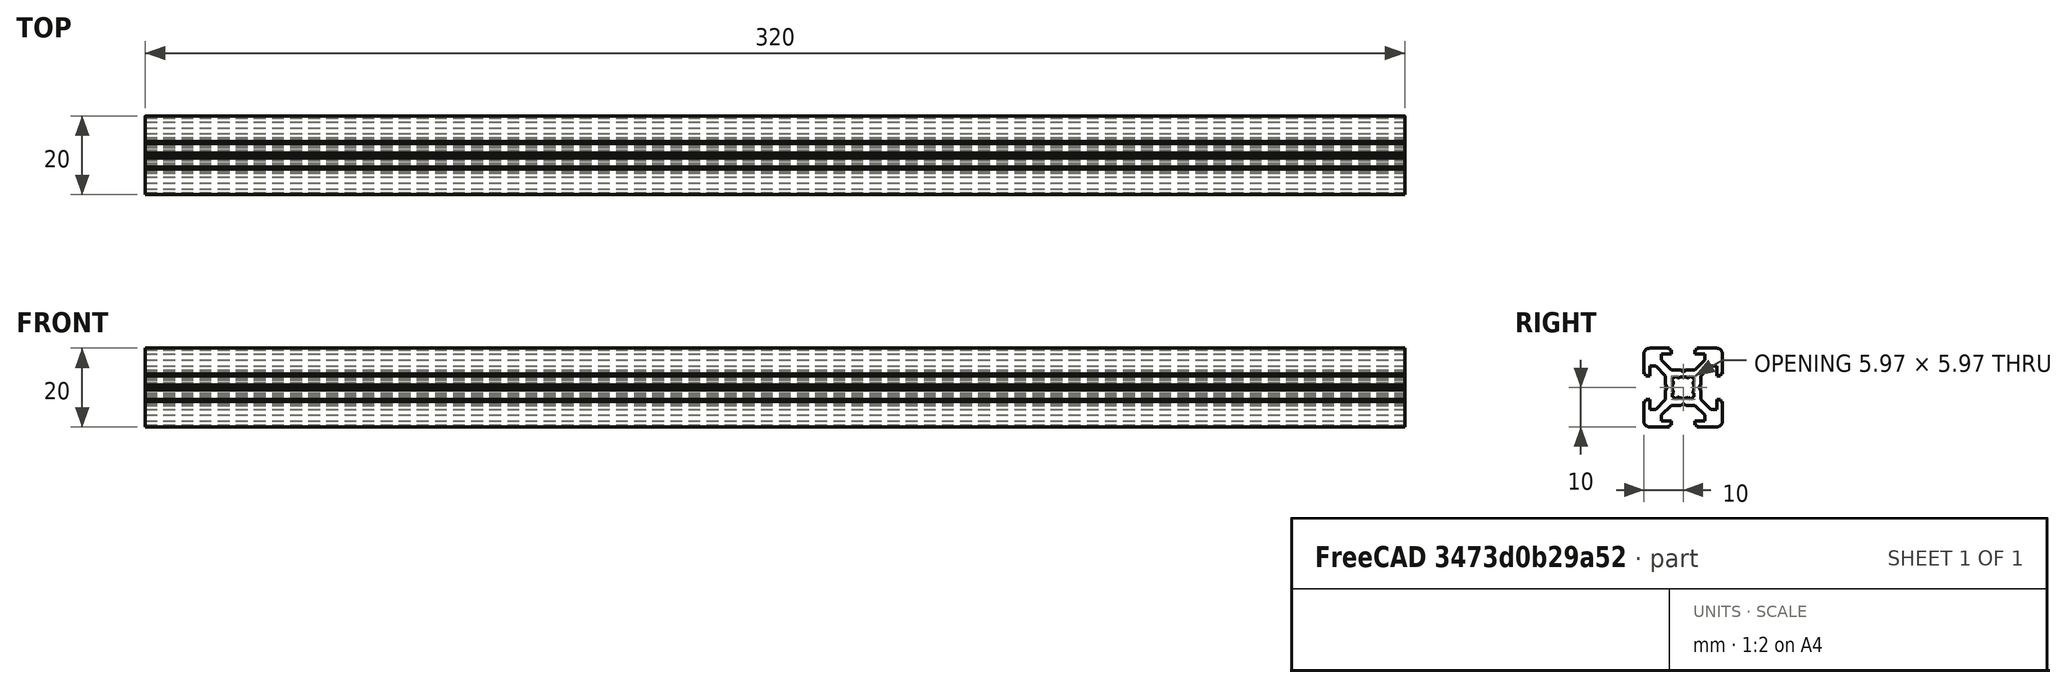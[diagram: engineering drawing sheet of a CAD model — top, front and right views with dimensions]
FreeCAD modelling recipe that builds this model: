
FCSTD DOCUMENT  (FreeCAD 0.19R)
Label: Tslot32
License: All rights reserved
LicenseURL: http://en.wikipedia.org/wiki/All_rights_reserved
objects: Sketcher::SketchObject×1, PartDesign::Pad×1, PartDesign::Body×1
note: 4 computed .brp shape members not serialized (recipe doc carries the construction recipe); baked Part::Feature solids carry a one-line shape summary decoded from their .brp

FEATURE [Sketcher::SketchObject] Sketch  label="T-Slot-Skizze"
  FullyConstrained = true
  MapMode = 5
  Placement = pos=(0,0,0) rot=(0.57735,0.57735,0.57735;2.0944rad)
  Support = -> [YZ_Plane]
  sketch-geometry (98):
    g0: LineSegment StartX=0 StartY=4.1 StartZ=0 EndX=0.65 EndY=4.5 EndZ=0
    g1: LineSegment StartX=0.65 StartY=4.5 StartZ=0 EndX=3 EndY=4.5 EndZ=0
    g2: LineSegment StartX=3 StartY=4.5 StartZ=0 EndX=5.5 EndY=7 EndZ=0
    g3: LineSegment StartX=5.5 StartY=7 StartZ=0 EndX=5.5 EndY=8.5 EndZ=0
    g4: LineSegment StartX=5.5 StartY=8.5 StartZ=0 EndX=3 EndY=8.5 EndZ=0
    g5: LineSegment StartX=3 StartY=8.5 StartZ=0 EndX=3 EndY=9.5 EndZ=0
    g6: LineSegment StartX=3 StartY=9.5 StartZ=0 EndX=3.5 EndY=9.5 EndZ=0
    g7: LineSegment StartX=3.5 StartY=9.5 StartZ=0 EndX=3.5 EndY=10 EndZ=0
    g8: LineSegment StartX=3.5 StartY=10 StartZ=0 EndX=8.5 EndY=10 EndZ=0
    g9: LineSegment StartX=10 StartY=8.5 StartZ=0 EndX=10 EndY=3.5 EndZ=0
    g10: LineSegment StartX=10 StartY=3.5 StartZ=0 EndX=9.5 EndY=3.5 EndZ=0
    g11: LineSegment StartX=9.5 StartY=3.5 StartZ=0 EndX=9.5 EndY=3 EndZ=0
    g12: LineSegment StartX=9.5 StartY=3 StartZ=0 EndX=8.5 EndY=3 EndZ=0
    g13: LineSegment StartX=8.5 StartY=3 StartZ=0 EndX=8.5 EndY=5.5 EndZ=0
    g14: LineSegment StartX=8.5 StartY=5.5 StartZ=0 EndX=7 EndY=5.5 EndZ=0
    g15: LineSegment StartX=7 StartY=5.5 StartZ=0 EndX=4.5 EndY=3 EndZ=0
    g16: LineSegment StartX=4.5 StartY=3 StartZ=0 EndX=4.5 EndY=0.65 EndZ=0
    g17: LineSegment StartX=4.5 StartY=0.65 StartZ=0 EndX=4.1 EndY=0 EndZ=0
    g18: ArcOfCircle CenterX=8.5 CenterY=8.5 CenterZ=0 NormalX=0 NormalY=0 NormalZ=1 AngleXU=0 Radius=1.5 StartAngle=0 EndAngle=1.5708
    g19: LineSegment StartX=0 StartY=-4.1 StartZ=0 EndX=0.65 EndY=-4.5 EndZ=0
    g20: LineSegment StartX=0.65 StartY=-4.5 StartZ=0 EndX=3 EndY=-4.5 EndZ=0
    g21: LineSegment StartX=3 StartY=-4.5 StartZ=0 EndX=5.5 EndY=-7 EndZ=0
    g22: LineSegment StartX=5.5 StartY=-7 StartZ=0 EndX=5.5 EndY=-8.5 EndZ=0
    g23: LineSegment StartX=5.5 StartY=-8.5 StartZ=0 EndX=3 EndY=-8.5 EndZ=0
    g24: LineSegment StartX=3 StartY=-8.5 StartZ=0 EndX=3 EndY=-9.5 EndZ=0
    g25: LineSegment StartX=3 StartY=-9.5 StartZ=0 EndX=3.5 EndY=-9.5 EndZ=0
    g26: LineSegment StartX=3.5 StartY=-9.5 StartZ=0 EndX=3.5 EndY=-10 EndZ=0
    g27: LineSegment StartX=3.5 StartY=-10 StartZ=0 EndX=8.5 EndY=-10 EndZ=0
    g28: LineSegment StartX=10 StartY=-8.5 StartZ=0 EndX=10 EndY=-3.5 EndZ=0
    g29: LineSegment StartX=10 StartY=-3.5 StartZ=0 EndX=9.5 EndY=-3.5 EndZ=0
    g30: LineSegment StartX=9.5 StartY=-3.5 StartZ=0 EndX=9.5 EndY=-3 EndZ=0
    g31: LineSegment StartX=9.5 StartY=-3 StartZ=0 EndX=8.5 EndY=-3 EndZ=0
    g32: LineSegment StartX=8.5 StartY=-3 StartZ=0 EndX=8.5 EndY=-5.5 EndZ=0
    g33: LineSegment StartX=8.5 StartY=-5.5 StartZ=0 EndX=7 EndY=-5.5 EndZ=0
    g34: LineSegment StartX=7 StartY=-5.5 StartZ=0 EndX=4.5 EndY=-3 EndZ=0
    g35: LineSegment StartX=4.5 StartY=-3 StartZ=0 EndX=4.5 EndY=-0.65 EndZ=0
    g36: ArcOfCircle CenterX=8.5 CenterY=-8.5 CenterZ=0 NormalX=0 NormalY=0 NormalZ=1 AngleXU=0 Radius=1.5 StartAngle=4.71239 EndAngle=6.28319
    g37: LineSegment StartX=4.5 StartY=-0.65 StartZ=0 EndX=4.1 EndY=0 EndZ=0
    g38: LineSegment StartX=0 StartY=-4.1 StartZ=0 EndX=-0.65 EndY=-4.5 EndZ=0
    g39: LineSegment StartX=-0.65 StartY=-4.5 StartZ=0 EndX=-3 EndY=-4.5 EndZ=0
    g40: LineSegment StartX=-3 StartY=-4.5 StartZ=0 EndX=-5.5 EndY=-7 EndZ=0
    g41: LineSegment StartX=-5.5 StartY=-7 StartZ=0 EndX=-5.5 EndY=-8.5 EndZ=0
    g42: LineSegment StartX=-5.5 StartY=-8.5 StartZ=0 EndX=-3 EndY=-8.5 EndZ=0
    g43: LineSegment StartX=-3 StartY=-8.5 StartZ=0 EndX=-3 EndY=-9.5 EndZ=0
    g44: LineSegment StartX=-3 StartY=-9.5 StartZ=0 EndX=-3.5 EndY=-9.5 EndZ=0
    g45: LineSegment StartX=-3.5 StartY=-9.5 StartZ=0 EndX=-3.5 EndY=-10 EndZ=0
    g46: LineSegment StartX=-3.5 StartY=-10 StartZ=0 EndX=-8.5 EndY=-10 EndZ=0
    g47: LineSegment StartX=-10 StartY=-8.5 StartZ=0 EndX=-10 EndY=-3.5 EndZ=0
    g48: LineSegment StartX=-10 StartY=-3.5 StartZ=0 EndX=-9.5 EndY=-3.5 EndZ=0
    g49: LineSegment StartX=-9.5 StartY=-3.5 StartZ=0 EndX=-9.5 EndY=-3 EndZ=0
    g50: LineSegment StartX=-9.5 StartY=-3 StartZ=0 EndX=-8.5 EndY=-3 EndZ=0
    g51: LineSegment StartX=-8.5 StartY=-3 StartZ=0 EndX=-8.5 EndY=-5.5 EndZ=0
    g52: LineSegment StartX=-8.5 StartY=-5.5 StartZ=0 EndX=-7 EndY=-5.5 EndZ=0
    g53: LineSegment StartX=-7 StartY=-5.5 StartZ=0 EndX=-4.5 EndY=-3 EndZ=0
    g54: LineSegment StartX=-4.5 StartY=-3 StartZ=0 EndX=-4.5 EndY=-0.65 EndZ=0
    g55: ArcOfCircle CenterX=-8.5 CenterY=-8.5 CenterZ=0 NormalX=0 NormalY=0 NormalZ=1 AngleXU=0 Radius=1.5 StartAngle=3.14159 EndAngle=4.71239
    g56: LineSegment StartX=-4.5 StartY=-0.65 StartZ=0 EndX=-4.1 EndY=0 EndZ=0
    g57: LineSegment StartX=-0.65 StartY=4.5 StartZ=0 EndX=-3 EndY=4.5 EndZ=0
    g58: LineSegment StartX=-3 StartY=4.5 StartZ=0 EndX=-5.5 EndY=7 EndZ=0
    g59: LineSegment StartX=-5.5 StartY=7 StartZ=0 EndX=-5.5 EndY=8.5 EndZ=0
    g60: LineSegment StartX=-5.5 StartY=8.5 StartZ=0 EndX=-3 EndY=8.5 EndZ=0
    g61: LineSegment StartX=-3 StartY=8.5 StartZ=0 EndX=-3 EndY=9.5 EndZ=0
    g62: LineSegment StartX=-3 StartY=9.5 StartZ=0 EndX=-3.5 EndY=9.5 EndZ=0
    g63: LineSegment StartX=-3.5 StartY=9.5 StartZ=0 EndX=-3.5 EndY=10 EndZ=0
    g64: LineSegment StartX=-3.5 StartY=10 StartZ=0 EndX=-8.5 EndY=10 EndZ=0
    g65: LineSegment StartX=-10 StartY=8.5 StartZ=0 EndX=-10 EndY=3.5 EndZ=0
    g66: LineSegment StartX=-10 StartY=3.5 StartZ=0 EndX=-9.5 EndY=3.5 EndZ=0
    g67: LineSegment StartX=-9.5 StartY=3.5 StartZ=0 EndX=-9.5 EndY=3 EndZ=0
    g68: LineSegment StartX=-9.5 StartY=3 StartZ=0 EndX=-8.5 EndY=3 EndZ=0
    g69: LineSegment StartX=-8.5 StartY=3 StartZ=0 EndX=-8.5 EndY=5.5 EndZ=0
    g70: LineSegment StartX=-8.5 StartY=5.5 StartZ=0 EndX=-7 EndY=5.5 EndZ=0
    g71: LineSegment StartX=-7 StartY=5.5 StartZ=0 EndX=-4.5 EndY=3 EndZ=0
    g72: LineSegment StartX=-4.5 StartY=3 StartZ=0 EndX=-4.5 EndY=0.65 EndZ=0
    g73: ArcOfCircle CenterX=-8.5 CenterY=8.5 CenterZ=0 NormalX=0 NormalY=0 NormalZ=1 AngleXU=0 Radius=1.5 StartAngle=1.5708 EndAngle=3.14159
    g74: LineSegment StartX=-4.5 StartY=0.65 StartZ=0 EndX=-4.1 EndY=0 EndZ=0
    g75: LineSegment StartX=0 StartY=4.1 StartZ=0 EndX=-0.65 EndY=4.5 EndZ=0
    g76: Circle CenterX=0 CenterY=0 CenterZ=0 NormalX=0 NormalY=0 NormalZ=1 AngleXU=0 Radius=3.55
    g77: Circle CenterX=0 CenterY=0 CenterZ=0 NormalX=0 NormalY=0 NormalZ=1 AngleXU=0 Radius=2.75
    g78: LineSegment StartX=1.3405 StartY=2.40116 StartZ=0 EndX=1.92324 EndY=2.9839 EndZ=0
    g79: LineSegment StartX=1.92324 StartY=2.9839 StartZ=0 EndX=2.9839 EndY=1.92324 EndZ=0
    g80: LineSegment StartX=2.9839 StartY=1.92324 StartZ=0 EndX=2.40116 EndY=1.3405 EndZ=0
    g81: ArcOfCircle CenterX=0 CenterY=0 CenterZ=0 NormalX=0 NormalY=0 NormalZ=1 AngleXU=0 Radius=2.75 StartAngle=0 EndAngle=0.509172
    g82: ArcOfCircle CenterX=0 CenterY=0 CenterZ=0 NormalX=0 NormalY=0 NormalZ=1 AngleXU=0 Radius=2.75 StartAngle=1.06162 EndAngle=1.5708
    g83: LineSegment StartX=-1.3405 StartY=2.40116 StartZ=0 EndX=-1.92324 EndY=2.9839 EndZ=0
    g84: LineSegment StartX=-1.92324 StartY=2.9839 StartZ=0 EndX=-2.9839 EndY=1.92324 EndZ=0
    g85: LineSegment StartX=-2.9839 StartY=1.92324 StartZ=0 EndX=-2.40116 EndY=1.3405 EndZ=0
    g86: ArcOfCircle CenterX=-1.3e-15 CenterY=6e-16 CenterZ=0 NormalX=0 NormalY=0 NormalZ=1 AngleXU=0 Radius=2.75 StartAngle=2.63242 EndAngle=3.14159
    g87: ArcOfCircle CenterX=-1.3e-15 CenterY=6e-16 CenterZ=0 NormalX=0 NormalY=0 NormalZ=1 AngleXU=0 Radius=2.75 StartAngle=1.5708 EndAngle=2.07997
    g88: LineSegment StartX=-1.34051 StartY=-2.40115 StartZ=0 EndX=-1.92325 EndY=-2.98389 EndZ=0
    g89: LineSegment StartX=-1.92325 StartY=-2.98389 StartZ=0 EndX=-2.9839 EndY=-1.92323 EndZ=0
    g90: LineSegment StartX=-2.9839 StartY=-1.92323 StartZ=0 EndX=-2.40116 EndY=-1.34049 EndZ=0
    g91: ArcOfCircle CenterX=-3e-16 CenterY=2e-16 CenterZ=0 NormalX=0 NormalY=0 NormalZ=1 AngleXU=0 Radius=2.75 StartAngle=3.14159 EndAngle=3.65076
    g92: ArcOfCircle CenterX=-3e-16 CenterY=2e-16 CenterZ=0 NormalX=0 NormalY=0 NormalZ=1 AngleXU=0 Radius=2.75 StartAngle=4.20321 EndAngle=4.71239
    g93: LineSegment StartX=1.34051 StartY=-2.40115 StartZ=0 EndX=1.92325 EndY=-2.98389 EndZ=0
    g94: LineSegment StartX=1.92325 StartY=-2.98389 StartZ=0 EndX=2.9839 EndY=-1.92323 EndZ=0
    g95: LineSegment StartX=2.9839 StartY=-1.92323 StartZ=0 EndX=2.40116 EndY=-1.34049 EndZ=0
    g96: ArcOfCircle CenterX=3e-16 CenterY=2e-16 CenterZ=0 NormalX=0 NormalY=0 NormalZ=1 AngleXU=0 Radius=2.75 StartAngle=4.71239 EndAngle=5.22156
    g97: ArcOfCircle CenterX=3e-16 CenterY=2e-16 CenterZ=0 NormalX=0 NormalY=0 NormalZ=1 AngleXU=0 Radius=2.75 StartAngle=5.77402 EndAngle=6.28319
  constraints (291):
    c: PointOnObject(g0,g-2)
    c: Coincident(g0,g1)
    c: Horizontal(g1)
    c: Coincident(g1,g2)
    c: Coincident(g2,g3)
    c: Vertical(g3)
    c: Coincident(g3,g4)
    c: Horizontal(g4)
    c: Coincident(g4,g5)
    c: Vertical(g5)
    c: Coincident(g5,g6)
    c: Horizontal(g6)
    c: Coincident(g6,g7)
    c: Coincident(g7,g8)
    c: Horizontal(g8)
    c: Vertical(g7)
    c: DistanceX(g-1,g5) = 3
    c: DistanceY(g4,g7) = 1.5
    c: DistanceY(g0,g7) = 5.5
    c: DistanceY(g3,g3) = 1.5
    c: DistanceY(g4,g5) = 1
    c: DistanceX(g-1,g1) = 3
    c: DistanceX(g-1,g7) = 3.5
    c: DistanceX(g0,g0) = 0.65
    c: DistanceY(g0,g0) = 0.4
    c: DistanceX(g-1,g3) = 5.5
    c: Vertical(g9)
    c: Coincident(g9,g10)
    c: Coincident(g10,g11)
    c: Coincident(g11,g12)
    c: Coincident(g12,g13)
    c: Vertical(g13)
    c: Coincident(g13,g14)
    c: Horizontal(g14)
    c: Coincident(g14,g15)
    c: Coincident(g15,g16)
    c: Vertical(g16)
    c: Coincident(g16,g17)
    c: PointOnObject(g17,g-1)
    c: Horizontal(g10)
    c: Horizontal(g12)
    c: Vertical(g11)
    c: Equal(g17,g0)
    c: Equal(g1,g16)
    c: Equal(g15,g2)
    c: Equal(g3,g14)
    c: Equal(g13,g4)
    c: Equal(g12,g5)
    c: Parallel(g15,g2)
    c: Equal(g11,g6)
    c: Equal(g10,g7)
    c: Equal(g9,g8)
    c: Tangent(g8,g18) = 1.5708
    c: Tangent(g9,g18) = 1.5708
    c: Radius(g18) = 1.5
    c: DistanceY(g-1,g8) = 10
    c: DistanceX(g-1,g9) = 10
    c: Coincident(g19,g20)
    c: Horizontal(g20)
    c: Coincident(g20,g21)
    c: Coincident(g21,g22)
    c: Vertical(g22)
    c: Coincident(g22,g23)
    c: Horizontal(g23)
    c: Coincident(g23,g24)
    c: Vertical(g24)
    c: Coincident(g24,g25)
    c: Horizontal(g25)
    c: Coincident(g25,g26)
    c: Coincident(g26,g27)
    c: Horizontal(g27)
    c: Vertical(g26)
    c: Vertical(g28)
    c: Coincident(g28,g29)
    c: Coincident(g29,g30)
    c: Coincident(g30,g31)
    c: Coincident(g31,g32)
    c: Vertical(g32)
    c: Coincident(g32,g33)
    c: Horizontal(g33)
    c: Coincident(g33,g34)
    c: Coincident(g34,g35)
    c: Vertical(g35)
    c: Coincident(g35,g37)
    c: Horizontal(g29)
    c: Horizontal(g31)
    c: Vertical(g30)
    c: Equal(g37,g19)
    c: Equal(g20,g35)
    c: Equal(g34,g21)
    c: Equal(g22,g33)
    c: Equal(g32,g23)
    c: Equal(g31,g24)
    c: Parallel(g34,g21)
    c: Equal(g30,g25)
    c: Equal(g29,g26)
    c: Equal(g28,g27)
    c: Tangent(g27,g36) = -1.5708
    c: Tangent(g28,g36) = -1.5708
    c: Radius(g36) = 1.5
    c: Equal(g9,g28)
    c: Equal(g12,g31)
    c: DistanceX(g-1,g28) = 10
    c: DistanceY(g27,g-1) = 10
    c: DistanceY(g30,g-1) = 3
    c: Equal(g33,g14)
    c: Equal(g35,g16)
    c: Equal(g17,g37)
    c: Coincident(g37,g17)
    c: Equal(g15,g34)
    c: PointOnObject(g19,g-2)
    c: DistanceY(g34,g-1) = 3
    c: DistanceX(g-1,g20) = 3
    c: Coincident(g38,g39)
    c: Horizontal(g39)
    c: Coincident(g39,g40)
    c: Coincident(g40,g41)
    c: Vertical(g41)
    c: Coincident(g41,g42)
    c: Horizontal(g42)
    c: Coincident(g42,g43)
    c: Vertical(g43)
    c: Coincident(g43,g44)
    c: Horizontal(g44)
    c: Coincident(g44,g45)
    c: Coincident(g45,g46)
    c: Horizontal(g46)
    c: Vertical(g45)
    c: Vertical(g47)
    c: Coincident(g47,g48)
    c: Coincident(g48,g49)
    c: Coincident(g49,g50)
    c: Coincident(g50,g51)
    c: Vertical(g51)
    c: Coincident(g51,g52)
    c: Horizontal(g52)
    c: Coincident(g52,g53)
    c: Coincident(g53,g54)
    c: Vertical(g54)
    c: Coincident(g54,g56)
    c: Horizontal(g48)
    c: Horizontal(g50)
    c: Vertical(g49)
    c: Equal(g39,g54)
    c: Equal(g53,g40)
    c: Equal(g41,g52)
    c: Equal(g51,g42)
    c: Equal(g50,g43)
    c: Parallel(g53,g40)
    c: Equal(g49,g44)
    c: Equal(g48,g45)
    c: Equal(g47,g46)
    c: Tangent(g46,g55) = 1.5708
    c: Tangent(g47,g55) = 1.5708
    c: Radius(g55) = 1.5
    c: Coincident(g38,g19)
    c: DistanceX(g39,g-1) = 3
    c: DistanceX(g38,g19) = 0.65
    c: DistanceY(g38,g19) = 0.4
    c: PointOnObject(g56,g-1)
    c: Equal(g56,g38)
    c: DistanceY(g53,g-1) = 3
    c: Equal(g22,g41)
    c: Equal(g42,g23)
    c: Equal(g24,g43)
    c: Equal(g25,g44)
    c: Equal(g26,g45)
    c: DistanceY(g46,g-1) = 10
    c: DistanceX(g47,g-1) = 10
    c: Coincident(g75,g57)
    c: Horizontal(g57)
    c: Coincident(g57,g58)
    c: Coincident(g58,g59)
    c: Vertical(g59)
    c: Coincident(g59,g60)
    c: Horizontal(g60)
    c: Coincident(g60,g61)
    c: Vertical(g61)
    c: Coincident(g61,g62)
    c: Horizontal(g62)
    c: Coincident(g62,g63)
    c: Coincident(g63,g64)
    c: Horizontal(g64)
    c: Vertical(g63)
    c: Vertical(g65)
    c: Coincident(g65,g66)
    c: Coincident(g66,g67)
    c: Coincident(g67,g68)
    c: Coincident(g68,g69)
    c: Vertical(g69)
    c: Coincident(g69,g70)
    c: Horizontal(g70)
    c: Coincident(g70,g71)
    c: Coincident(g71,g72)
    c: Vertical(g72)
    c: Coincident(g72,g74)
    c: Horizontal(g66)
    c: Horizontal(g68)
    c: Vertical(g67)
    c: Equal(g57,g72)
    c: Equal(g71,g58)
    c: Equal(g59,g70)
    c: Equal(g69,g60)
    c: Equal(g68,g61)
    c: Parallel(g71,g58)
    c: Equal(g67,g62)
    c: Equal(g66,g63)
    c: Equal(g65,g64)
    c: Tangent(g64,g73) = -1.5708
    c: Tangent(g65,g73) = -1.5708
    c: Radius(g73) = 1.5
    c: Equal(g74,g75)
    c: Coincident(g56,g74)
    c: Coincident(g0,g75)
    c: Equal(g0,g75)
    c: Equal(g1,g57)
    c: Equal(g2,g58)
    c: Equal(g3,g59)
    c: Equal(g4,g60)
    c: Equal(g5,g61)
    c: Equal(g6,g62)
    c: Equal(g7,g63)
    c: Equal(g8,g64)
    c: DistanceX(g65,g-1) = 10
    c: Coincident(g76,g-1)
    c: Coincident(g77,g-1)
    c: Radius(g76) = 3.55
    c: Radius(g77) = 2.75
    c: PointOnObject(g78,g77)
    c: PointOnObject(g78,g76)
    c: Coincident(g78,g79)
    c: PointOnObject(g79,g76)
    c: Coincident(g79,g80)
    c: PointOnObject(g80,g77)
    c: Coincident(g81,g-1)
    c: Coincident(g81,g80)
    c: Coincident(g82,g81)
    c: Coincident(g82,g78)
    c: Parallel(g78,g80)
    c: Parallel(g78,g2)
    c: Distance(g79) = 1.5
    c: Distance(g78,g80) = 1.5
    c: PointOnObject(g82,g-2)
    c: PointOnObject(g81,g-1)
    c: Coincident(g83,g84)
    c: Coincident(g84,g85)
    c: Coincident(g86,g85)
    c: Coincident(g87,g86)
    c: Coincident(g87,g83)
    c: Parallel(g83,g85)
    c: Distance(g84) = 1.5
    c: Distance(g83,g85) = 1.5
    c: Coincident(g82,g87)
    c: PointOnObject(g86,g-1)
    c: PointOnObject(g83,g76)
    c: PointOnObject(g83,g77)
    c: PointOnObject(g85,g77)
    c: PointOnObject(g84,g76)
    c: PointOnObject(g86,g77)
    c: Parallel(g85,g71)
    c: Coincident(g88,g89)
    c: Coincident(g89,g90)
    c: Coincident(g91,g90)
    c: Coincident(g92,g91)
    c: Coincident(g92,g88)
    c: Parallel(g88,g90)
    c: Distance(g89) = 1.5
    c: Distance(g88,g90) = 1.5
    c: PointOnObject(g88,g77)
    c: PointOnObject(g90,g77)
    c: Coincident(g86,g91)
    c: PointOnObject(g89,g76)
    c: PointOnObject(g88,g76)
    c: PointOnObject(g92,g-2)
    c: PointOnObject(g92,g77)
    c: Parallel(g88,g40)
    c: Coincident(g93,g94)
    c: Coincident(g94,g95)
    c: Coincident(g97,g95)
    c: Coincident(g96,g97)
    c: Coincident(g96,g93)
    c: Parallel(g93,g95)
    c: Distance(g94) = 1.5
    c: Distance(g93,g95) = 1.5
    c: Coincident(g81,g97)
    c: Coincident(g92,g96)
    c: PointOnObject(g93,g77)
    c: PointOnObject(g95,g77)
    c: PointOnObject(g94,g76)
    c: PointOnObject(g93,g76)
    c: Parallel(g93,g21)
FEATURE [PartDesign::Pad] Pad  label="T-Slot-Element"
  Direction = (1,1,1)
  Length = 320
  Length2 = 100
  Placement = pos=(0,0,0) rot=(0.57735,0.57735,0.57735;2.0944rad)
  Profile = -> Sketch
  Type = 0
FEATURE [PartDesign::Body] Body  label="T-Slot-Profil 20x20"
  Group = -> [Sketch,Pad]
  Origin = -> Origin
  Tip = -> Pad
